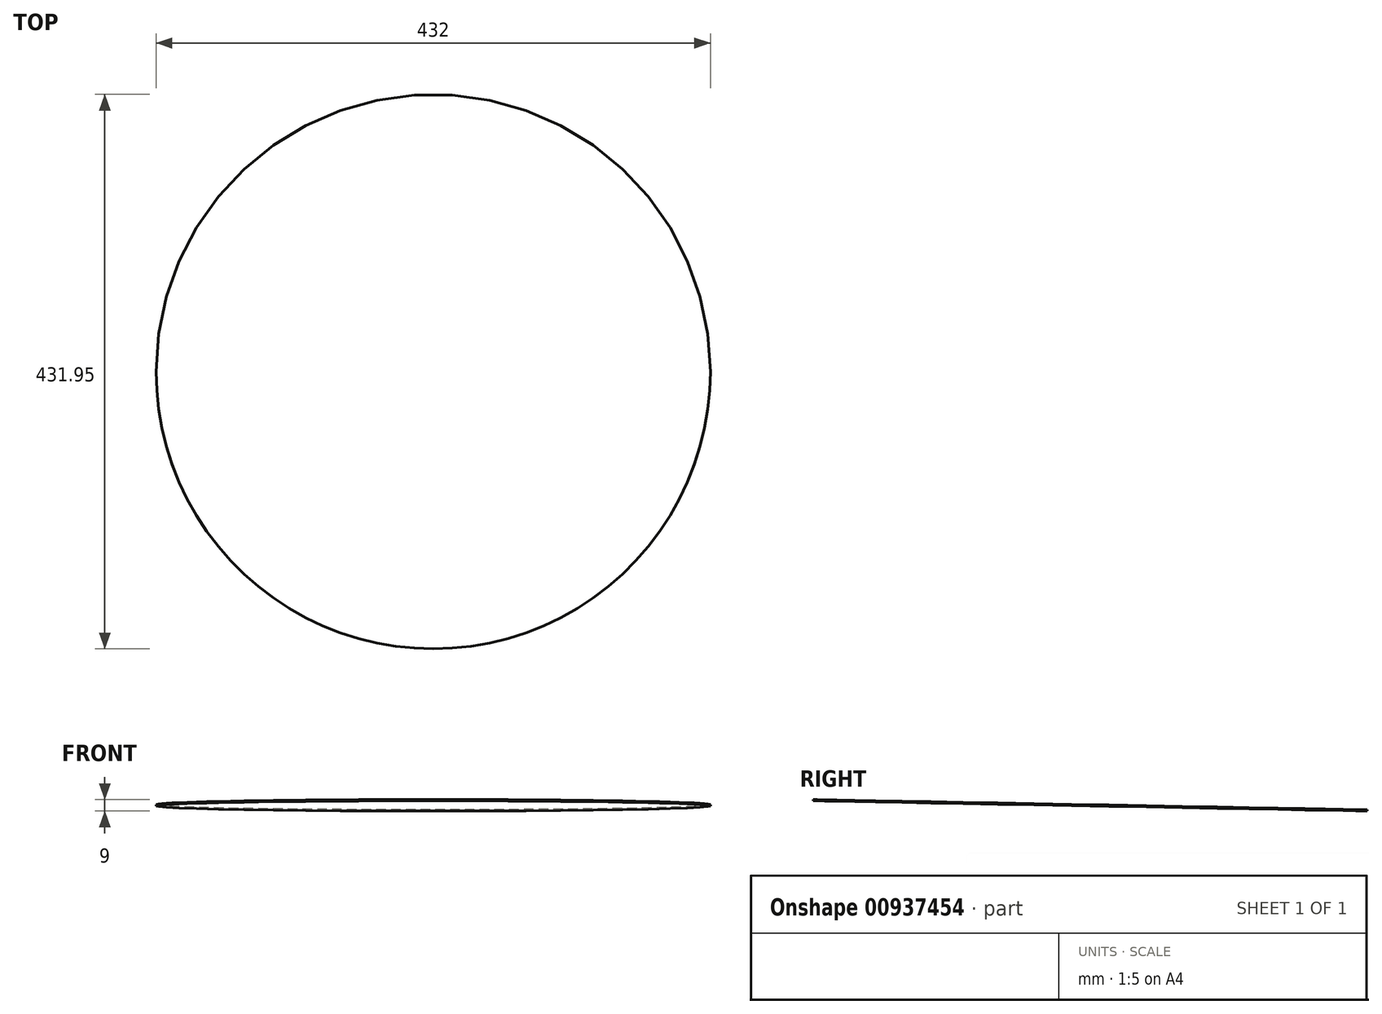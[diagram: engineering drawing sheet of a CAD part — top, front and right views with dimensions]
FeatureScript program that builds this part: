
annotation { "Feature Type Name" : "Feature", "Feature Type Description" : "" }
export const myFeature = defineFeature(function(context is Context, id is Id, definition is map)
    precondition{}
    {
        {
            var Q0;
            Q0=qCreatedBy(makeId("Top.planeOp"),FACE);
            var sketch = newSketch(context, id + "F0", { "sketchPlane" : qUnion([Q0])});
            skCircle(sketch, "E0", {"center": v(0, 216) * mm, "radius": 216 * mm});
            skLineSegment(sketch, "E1", {"start": v(-85.57, 0) * mm, "end": v(120.2, 0) * mm, "construction": true});
            skPoint(sketch, "E2", {"position": v(0, 432) * mm});
            skPoint(sketch, "E3.1.0", {"position": v(-55.9, 424.64) * mm});
            skPoint(sketch, "E3.2.0", {"position": v(-108, 403.06) * mm});
            skPoint(sketch, "E3.3.0", {"position": v(-152.74, 368.74) * mm});
            skPoint(sketch, "E3.4.0", {"position": v(-187.06, 324) * mm});
            skPoint(sketch, "E3.5.0", {"position": v(-208.64, 271.9) * mm});
            skPoint(sketch, "E3.6.0", {"position": v(-216, 216) * mm});
            skPoint(sketch, "E3.7.0", {"position": v(-208.64, 160.1) * mm});
            skPoint(sketch, "E3.8.0", {"position": v(-187.06, 108) * mm});
            skPoint(sketch, "E3.9.0", {"position": v(-152.74, 63.26) * mm});
            skPoint(sketch, "E3.10.0", {"position": v(-108, 28.94) * mm});
            skPoint(sketch, "E3.11.0", {"position": v(-55.9, 7.36) * mm});
            skPoint(sketch, "E3.12.0", {"position": v(0, 0) * mm});
            skPoint(sketch, "E3.13.0", {"position": v(55.9, 7.36) * mm});
            skPoint(sketch, "E3.14.0", {"position": v(108, 28.94) * mm});
            skPoint(sketch, "E3.15.0", {"position": v(152.74, 63.26) * mm});
            skPoint(sketch, "E3.16.0", {"position": v(187.06, 108) * mm});
            skPoint(sketch, "E3.17.0", {"position": v(208.64, 160.1) * mm});
            skPoint(sketch, "E3.18.0", {"position": v(216, 216) * mm});
            skPoint(sketch, "E4.0.19.0", {"position": v(208.64, 271.9) * mm});
            skPoint(sketch, "E4.0.20.0", {"position": v(187.06, 324) * mm});
            skPoint(sketch, "E5.0.21.0", {"position": v(152.74, 368.74) * mm});
            skPoint(sketch, "E6.0.22.0", {"position": v(108, 403.06) * mm});
            skPoint(sketch, "E7.0.23.0", {"position": v(55.9, 424.64) * mm});
            skSolve(sketch);
        }
        {
            var Q0;
            Q0=qCreatedBy(makeId("Right.planeOp"),FACE);
            var sketch = newSketch(context, id + "F1", { "sketchPlane" : qUnion([Q0])});
            skLineSegment(sketch, "E8.0", {"start": v(0, 0) * mm, "end": v(432, 0) * mm, "construction": true});
            skLineSegment(sketch, "E9", {"start": v(432, 0) * mm, "end": v(432, -8) * mm, "construction": true});
            skLineSegment(sketch, "E10", {"start": v(432, -8) * mm, "end": v(0, 0) * mm, "construction": true});
            skSolve(sketch);
        }
        {
            var Q0;
            Q0=sQuery(id+"F1.wireOp",EDGE,"E10");
            var Q1;
            Q1=sQuery(id+"F0.wireOp",EDGE,"E1");
            cPlane(context, id + "F2", {"entities" : qUnion([Q0, Q1]), "cplaneType" : CPlaneType.LINE_ANGLE, "offset" : 25 * mm, "angle" : 0 * degree, "width" : 150 * mm, "height" : 150 * mm});
        }
        {
            var Q0;
            Q0=qCreatedBy(id+"F2.planeOp",FACE);
            var sketch = newSketch(context, id + "F3", { "sketchPlane" : qUnion([Q0])});
            skCircle(sketch, "E11", {"center": v(0, 216) * mm, "radius": 216 * mm});
            skPoint(sketch, "E12", {"position": v(0, 432) * mm});
            skPoint(sketch, "E13.1.0", {"position": v(-55.9, 424.64) * mm});
            skPoint(sketch, "E13.2.0", {"position": v(-108, 403.06) * mm});
            skPoint(sketch, "E13.3.0", {"position": v(-152.74, 368.74) * mm});
            skPoint(sketch, "E13.4.0", {"position": v(-187.06, 324) * mm});
            skPoint(sketch, "E13.5.0", {"position": v(-208.64, 271.9) * mm});
            skPoint(sketch, "E13.6.0", {"position": v(-216, 216) * mm});
            skPoint(sketch, "E13.7.0", {"position": v(-208.64, 160.1) * mm});
            skPoint(sketch, "E13.8.0", {"position": v(-187.06, 108) * mm});
            skPoint(sketch, "E13.9.0", {"position": v(-152.74, 63.26) * mm});
            skPoint(sketch, "E13.10.0", {"position": v(-108, 28.94) * mm});
            skPoint(sketch, "E13.11.0", {"position": v(-55.9, 7.36) * mm});
            skPoint(sketch, "E13.12.0", {"position": v(0, 0) * mm});
            skPoint(sketch, "E13.13.0", {"position": v(55.9, 7.36) * mm});
            skPoint(sketch, "E13.14.0", {"position": v(108, 28.94) * mm});
            skPoint(sketch, "E13.15.0", {"position": v(152.74, 63.26) * mm});
            skPoint(sketch, "E13.16.0", {"position": v(187.06, 108) * mm});
            skPoint(sketch, "E13.17.0", {"position": v(208.64, 160.1) * mm});
            skPoint(sketch, "E13.18.0", {"position": v(216, 216) * mm});
            skPoint(sketch, "E14.0.19.0", {"position": v(208.64, 271.9) * mm});
            skPoint(sketch, "E14.0.20.0", {"position": v(187.06, 324) * mm});
            skPoint(sketch, "E14.0.21.0", {"position": v(152.74, 368.74) * mm});
            skPoint(sketch, "E14.0.22.0", {"position": v(108, 403.06) * mm});
            skPoint(sketch, "E14.0.23.0", {"position": v(55.9, 424.64) * mm});
            skSolve(sketch);
        }
        {
            var Q0;
            Q0=makeQuery(id+"F0.imprint","IMPRINT",FACE,{"disambiguationData":[TD([[makeQuery(id+"F0.imprint","IMPRINT",EDGE,{"derivedFrom":sQuery(id+"F0.wireOp",EDGE,"E0")}),1.0]])]});
            cPlane(context, id + "F4", {"entities" : qUnion([Q0]), "cplaneType" : CPlaneType.OFFSET, "offset" : 5 * mm, "width" : 150 * mm, "height" : 150 * mm});
        }
        {
            var Q0;
            Q0=makeQuery(id+"F0.imprint","IMPRINT",FACE,{"disambiguationData":[TD([[makeQuery(id+"F0.imprint","IMPRINT",EDGE,{"derivedFrom":sQuery(id+"F0.wireOp",EDGE,"E0")}),1.0]])]});
            var sketch = newSketch(context, id + "F5", { "sketchPlane" : qUnion([Q0])});
            skCircle(sketch, "E15.0", {"center": v(0, 216) * mm, "radius": 187.1 * mm, "construction": true});
            skPoint(sketch, "E16", {"position": v(0, 403.1) * mm});
            skLineSegment(sketch, "E17", {"start": v(0, 495.47) * mm, "end": v(0, 332.08) * mm, "construction": true});
            skLineSegment(sketch, "E18", {"start": v(0, 403.1) * mm, "end": v(53.43, 395.3) * mm});
            skLineSegment(sketch, "E19", {"start": v(53.43, 395.3) * mm, "end": v(98.16, 375.28) * mm});
            skLineSegment(sketch, "E20", {"start": v(98.16, 375.28) * mm, "end": v(138.2, 342.12) * mm});
            skLineSegment(sketch, "E21", {"start": v(138.2, 342.12) * mm, "end": v(166.44, 301.46) * mm});
            skLineSegment(sketch, "E22", {"start": v(166.44, 301.46) * mm, "end": v(186, 236.33) * mm});
            skLineSegment(sketch, "E23", {"start": v(186, 236.33) * mm, "end": v(180.84, 168.02) * mm});
            skLineSegment(sketch, "E24", {"start": v(180.84, 168.02) * mm, "end": v(159.87, 118.8) * mm});
            skLineSegment(sketch, "E25", {"start": v(159.87, 118.8) * mm, "end": v(140.97, 92.98) * mm});
            skLineSegment(sketch, "E26", {"start": v(0, 403.1) * mm, "end": v(-54.4, 395.02) * mm});
            skLineSegment(sketch, "E27", {"start": v(-54.4, 395.02) * mm, "end": v(-105.36, 370.61) * mm});
            skLineSegment(sketch, "E28", {"start": v(-105.36, 370.61) * mm, "end": v(-153.66, 322.75) * mm});
            skSolve(sketch);
        }
        {
            var Q0;
            Q0=makeQuery(id+"F3.imprint","IMPRINT",FACE,{"disambiguationData":[TD([[makeQuery(id+"F3.imprint","IMPRINT",EDGE,{"derivedFrom":sQuery(id+"F3.wireOp",EDGE,"E11")}),1.0]])]});
            extrude(context, id + "F6", {"entities" : qUnion([Q0]), "oppositeDirection" : true, "depth" : 1 * mm, "offsetDistance" : 25 * mm});
        }
        {
            var Q0;
            Q0=sQuery(id+"F5.wireOp",EDGE,"E28");
            var Q1;
            Q1=sQuery(id+"F5.wireOp",EDGE,"E27");
            var Q2;
            Q2=sQuery(id+"F5.wireOp",EDGE,"E26");
            var Q3;
            Q3=sQuery(id+"F5.wireOp",EDGE,"E18");
            var Q4;
            Q4=sQuery(id+"F5.wireOp",EDGE,"E19");
            var Q5;
            Q5=sQuery(id+"F5.wireOp",EDGE,"E20");
            var Q6;
            Q6=sQuery(id+"F5.wireOp",EDGE,"E21");
            var Q7;
            Q7=sQuery(id+"F5.wireOp",EDGE,"E22");
            var Q8;
            Q8=sQuery(id+"F5.wireOp",EDGE,"E23");
            var Q9;
            Q9=sQuery(id+"F5.wireOp",EDGE,"E24");
            var Q10;
            Q10=sQuery(id+"F5.wireOp",EDGE,"E25");
            var Q11;
            Q11=makeQuery(id+"F6.opExtrude","CAP_FACE",FACE,{"disambiguationData":[OSD([sQuery(id+"F3.wireOp",EDGE,"E11")])],"isStart":true});
            extrude(context, id + "F7", {"bodyType" : ToolBodyType.SURFACE, "surfaceEntities" : qUnion([Q0, Q1, Q2, Q3, Q4, Q5, Q6, Q7, Q8, Q9, Q10]), "endBound" : BoundingType.UP_TO_SURFACE, "oppositeDirection" : true, "depth" : 25 * mm, "endBoundEntityFace" : qUnion([Q11]), "offsetDistance" : 25 * mm});
        }
    });
